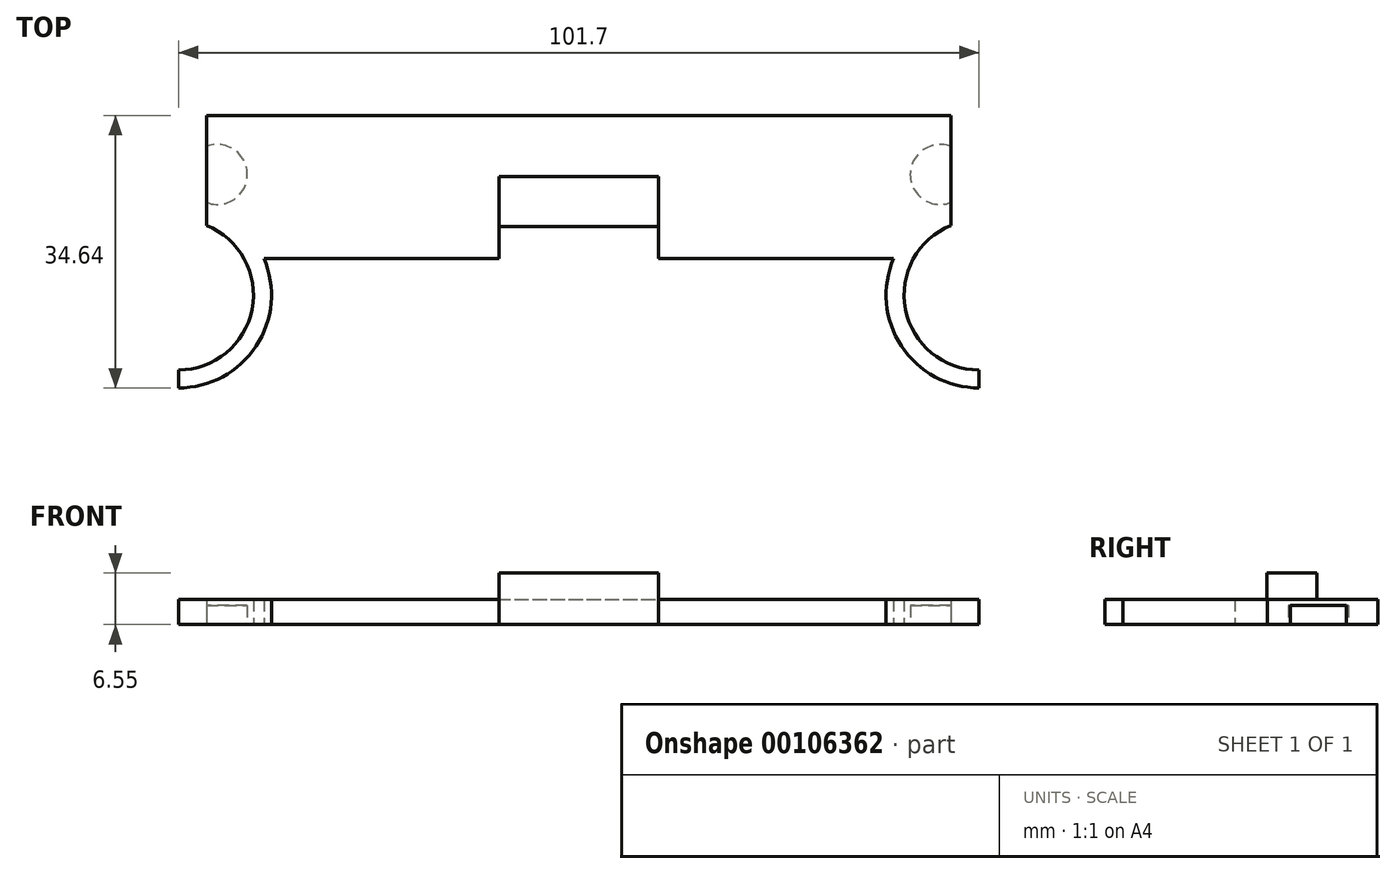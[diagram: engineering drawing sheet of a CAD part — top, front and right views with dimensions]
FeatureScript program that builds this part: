
annotation { "Feature Type Name" : "Feature", "Feature Type Description" : "" }
export const myFeature = defineFeature(function(context is Context, id is Id, definition is map)
    precondition{}
    {
        {
            var Q0;
            Q0=qCreatedBy(makeId("Top.planeOp"),FACE);
            var sketch = newSketch(context, id + "F0", { "sketchPlane" : qUnion([Q0])});
            skLineSegment(sketch, "E0.bottom", {"start": v(-47.29, 18.16) * mm, "end": v(47.29, 18.16) * mm});
            skLineSegment(sketch, "E0.top", {"start": v(-40, 0) * mm, "end": v(-10.16, 0) * mm});
            skLineSegment(sketch, "E0.left", {"start": v(-47.29, 18.16) * mm, "end": v(-47.29, 4.17) * mm});
            skLineSegment(sketch, "E0.right", {"start": v(47.29, 18.16) * mm, "end": v(47.29, 4.17) * mm});
            skArc(sketch, "E1", {"start": v(-50.85, -14.19) * mm, "mid": v(-41.5, -6.48) * mm, "end": v(-47.29, 4.17) * mm});
            skArc(sketch, "E2", {"start": v(-50.85, -16.48) * mm, "mid": v(-40.99, -11.16) * mm, "end": v(-40, 0) * mm});
            skLineSegment(sketch, "E3", {"start": v(-50.85, -14.19) * mm, "end": v(-50.85, -16.48) * mm});
            skArc(sketch, "E4.MirrorCS", {"start": v(50.85, -16.48) * mm, "mid": v(40.99, -11.16) * mm, "end": v(40, 0) * mm});
            skArc(sketch, "E5.MirrorCS", {"start": v(50.85, -14.19) * mm, "mid": v(41.5, -6.48) * mm, "end": v(47.29, 4.17) * mm});
            skLineSegment(sketch, "E6.MirrorCS", {"start": v(50.85, -14.19) * mm, "end": v(50.85, -16.48) * mm});
            skPoint(sketch, "E7.orphan", {"position": v(47.29, 0) * mm});
            skLineSegment(sketch, "E8.top", {"start": v(-10.16, 4.05) * mm, "end": v(10.16, 4.05) * mm});
            skLineSegment(sketch, "E8.left", {"start": v(-10.16, 0) * mm, "end": v(-10.16, 4.05) * mm});
            skLineSegment(sketch, "E8.right", {"start": v(10.16, 0) * mm, "end": v(10.16, 4.05) * mm});
            skLineSegment(sketch, "E9.trimOffspring", {"start": v(10.16, 0) * mm, "end": v(40, 0) * mm});
            skSolve(sketch);
        }
        {
            var Q0;
            Q0=qSketchRegion(id+"F0",true);
            extrude(context, id + "F1", {"entities" : qUnion([Q0]), "depth" : 3.17 * mm});
        }
        {
            var Q0;
            Q0=makeQuery(id+"F1.opExtrude","CAP_FACE",FACE,{"disambiguationData":[OSD([sQuery(id+"F0.wireOp",EDGE,"E0.bottom"),sQuery(id+"F0.wireOp",EDGE,"E0.top"),sQuery(id+"F0.wireOp",EDGE,"E0.left"),sQuery(id+"F0.wireOp",EDGE,"E0.right"),sQuery(id+"F0.wireOp",EDGE,"E1"),sQuery(id+"F0.wireOp",EDGE,"E2"),sQuery(id+"F0.wireOp",EDGE,"E3"),sQuery(id+"F0.wireOp",EDGE,"E4.MirrorCS"),sQuery(id+"F0.wireOp",EDGE,"E5.MirrorCS"),sQuery(id+"F0.wireOp",EDGE,"E6.MirrorCS"),sQuery(id+"F0.wireOp",EDGE,"E8.top"),sQuery(id+"F0.wireOp",EDGE,"E8.left"),sQuery(id+"F0.wireOp",EDGE,"E8.right"),sQuery(id+"F0.wireOp",EDGE,"E9.trimOffspring")])],"isStart":true});
            var sketch = newSketch(context, id + "F2", { "sketchPlane" : qUnion([Q0])});
            skArc(sketch, "E10", {"start": v(-47.29, -14.2) * mm, "mid": v(-42.1, -10.64) * mm, "end": v(-47.29, -7.1) * mm});
            skLineSegment(sketch, "E11", {"start": v(-47.29, -7.1) * mm, "end": v(-47.29, -14.2) * mm});
            skArc(sketch, "E12.MirrorCS", {"start": v(47.29, -14.2) * mm, "mid": v(42.1, -10.64) * mm, "end": v(47.29, -7.1) * mm});
            skLineSegment(sketch, "E13.MirrorCS", {"start": v(47.29, -7.1) * mm, "end": v(47.29, -14.2) * mm});
            skSolve(sketch);
        }
        {
            var Q0;
            Q0=qSketchRegion(id+"F2",true);
            extrude(context, id + "F3", {"entities" : qUnion([Q0]), "operationType" : NewBodyOperationType.REMOVE, "oppositeDirection" : true, "depth" : 2.41 * mm});
        }
        {
            var Q0;
            Q0=makeQuery(id+"F1.opExtrude","CAP_FACE",FACE,{"disambiguationData":[OSD([sQuery(id+"F0.wireOp",EDGE,"E0.bottom"),sQuery(id+"F0.wireOp",EDGE,"E0.top"),sQuery(id+"F0.wireOp",EDGE,"E0.left"),sQuery(id+"F0.wireOp",EDGE,"E0.right"),sQuery(id+"F0.wireOp",EDGE,"E1"),sQuery(id+"F0.wireOp",EDGE,"E2"),sQuery(id+"F0.wireOp",EDGE,"E3"),sQuery(id+"F0.wireOp",EDGE,"E4.MirrorCS"),sQuery(id+"F0.wireOp",EDGE,"E5.MirrorCS"),sQuery(id+"F0.wireOp",EDGE,"E6.MirrorCS"),sQuery(id+"F0.wireOp",EDGE,"E8.top"),sQuery(id+"F0.wireOp",EDGE,"E8.left"),sQuery(id+"F0.wireOp",EDGE,"E8.right"),sQuery(id+"F0.wireOp",EDGE,"E9.trimOffspring")])],"isStart":false});
            var sketch = newSketch(context, id + "F4", { "sketchPlane" : qUnion([Q0])});
            skLineSegment(sketch, "E14.bottom", {"start": v(-10.16, 4.05) * mm, "end": v(10.16, 4.05) * mm});
            skLineSegment(sketch, "E14.top", {"start": v(-10.16, 10.4) * mm, "end": v(10.16, 10.4) * mm});
            skLineSegment(sketch, "E14.left", {"start": v(-10.16, 4.05) * mm, "end": v(-10.16, 10.4) * mm});
            skLineSegment(sketch, "E14.right", {"start": v(10.16, 4.05) * mm, "end": v(10.16, 10.4) * mm});
            skSolve(sketch);
        }
        {
            var Q0;
            Q0 = qSketchRegion(id + "F4", true);
            extrude(context, id + "F5", {"entities" : qUnion([Q0]), "operationType" : NewBodyOperationType.ADD, "depth" : 3.38 * mm});
        }
    });
